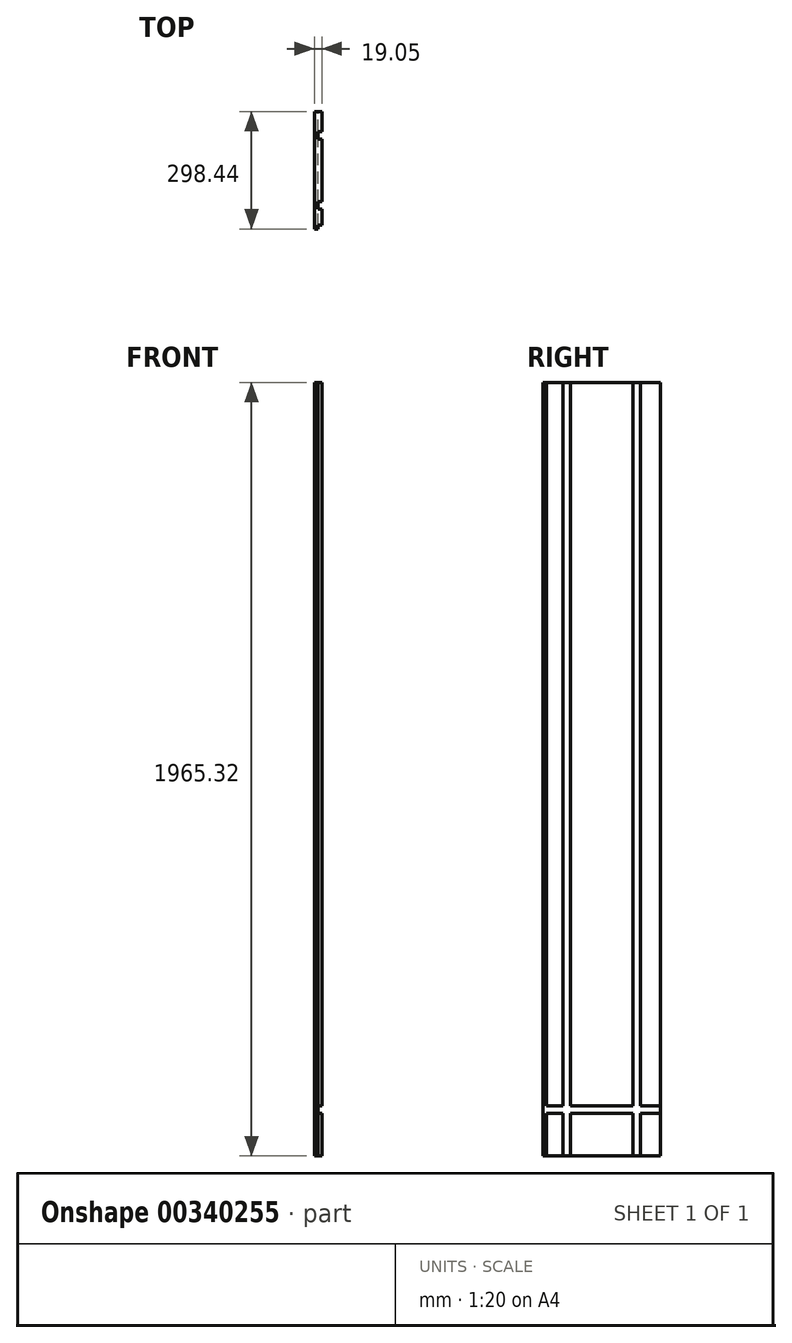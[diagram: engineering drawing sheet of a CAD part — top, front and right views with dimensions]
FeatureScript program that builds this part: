
annotation { "Feature Type Name" : "Feature", "Feature Type Description" : "" }
export const myFeature = defineFeature(function(context is Context, id is Id, definition is map)
    precondition{}
    {
        {
            var Q0;
            Q0=qCreatedBy(makeId("Right.planeOp"),FACE);
            var sketch = newSketch(context, id + "F0", { "sketchPlane" : qUnion([Q0])});
            skLineSegment(sketch, "E0.bottom", {"start": v(149.22, -982.66) * mm, "end": v(-149.23, -982.66) * mm});
            skLineSegment(sketch, "E0.top", {"start": v(149.22, 982.66) * mm, "end": v(-149.23, 982.66) * mm});
            skLineSegment(sketch, "E0.left", {"start": v(149.22, -982.66) * mm, "end": v(149.22, 982.66) * mm});
            skLineSegment(sketch, "E0.right", {"start": v(-149.23, -982.66) * mm, "end": v(-149.23, 982.66) * mm});
            skPoint(sketch, "E0.middle", {"position": v(0, 0) * mm});
            skSolve(sketch);
        }
        {
            var Q0;
            Q0=makeQuery(id+"F0.imprint","IMPRINT",FACE,{"disambiguationData":[TD([[makeQuery(id+"F0.imprint","IMPRINT",EDGE,{"derivedFrom":sQuery(id+"F0.wireOp",EDGE,"E0.bottom")}),-1.0]])]});
            extrude(context, id + "F1", {"entities" : qUnion([Q0]), "depth" : 19.05 * mm});
        }
        {
            var Q0;
            Q0=makeQuery(id+"F1.opExtrude","CAP_FACE",FACE,{"disambiguationData":[OSD([sQuery(id+"F0.wireOp",EDGE,"E0.bottom"),sQuery(id+"F0.wireOp",EDGE,"E0.top"),sQuery(id+"F0.wireOp",EDGE,"E0.left"),sQuery(id+"F0.wireOp",EDGE,"E0.right")])],"isStart":false});
            var sketch = newSketch(context, id + "F2", { "sketchPlane" : qUnion([Q0])});
            skLineSegment(sketch, "E1.bottom", {"start": v(-149.23, -855.66) * mm, "end": v(149.22, -855.66) * mm});
            skLineSegment(sketch, "E1.top", {"start": v(-149.23, -874.71) * mm, "end": v(149.22, -874.71) * mm});
            skLineSegment(sketch, "E1.left", {"start": v(-149.23, -855.66) * mm, "end": v(-149.23, -874.71) * mm});
            skLineSegment(sketch, "E1.right", {"start": v(149.22, -855.66) * mm, "end": v(149.22, -874.71) * mm});
            skSolve(sketch);
        }
        {
            var Q0;
            Q0 = qSketchRegion(id + "F2", true);
            extrude(context, id + "F3", {"entities" : qUnion([Q0]), "operationType" : NewBodyOperationType.REMOVE, "oppositeDirection" : true, "depth" : 9.52 * mm});
        }
        {
            var Q0;
            {var subQ0=sQuery(id+"F0.wireOp",EDGE,"E0.top");var subQ1=sQuery(id+"F0.wireOp",EDGE,"E0.left");var subQ2=sQuery(id+"F0.wireOp",EDGE,"E0.right");Q0=makeQuery(id+"F3.boolean.opBoolean","SPLIT",FACE,{"disambiguationData":[TD([makeQuery(id+"F1.opExtrude","SWEPT_FACE",FACE,{"disambiguationData":[OSD([subQ0])]})])],"derivedFrom":makeQuery(id+"F1.opExtrude","CAP_FACE",FACE,{"disambiguationData":[OSD([sQuery(id+"F0.wireOp",EDGE,"E0.bottom"),subQ0,subQ1,subQ2])],"isStart":false})});}
            var sketch = newSketch(context, id + "F4", { "sketchPlane" : qUnion([Q0])});
            skLineSegment(sketch, "E2.bottom", {"start": v(-98.43, 982.66) * mm, "end": v(-79.38, 982.66) * mm});
            skLineSegment(sketch, "E2.top", {"start": v(-98.43, -982.66) * mm, "end": v(-79.38, -982.66) * mm});
            skLineSegment(sketch, "E2.left", {"start": v(-98.43, 982.66) * mm, "end": v(-98.43, -982.66) * mm});
            skLineSegment(sketch, "E2.right", {"start": v(-79.38, 982.66) * mm, "end": v(-79.38, -982.66) * mm});
            skLineSegment(sketch, "E3", {"start": v(0, 982.66) * mm, "end": v(0, -982.66) * mm, "construction": true});
            skLineSegment(sketch, "E4.MirrorCS", {"start": v(98.43, -982.66) * mm, "end": v(79.38, -982.66) * mm});
            skLineSegment(sketch, "E5.MirrorCS", {"start": v(98.43, 982.66) * mm, "end": v(79.38, 982.66) * mm});
            skLineSegment(sketch, "E6.MirrorCS", {"start": v(79.38, 982.66) * mm, "end": v(79.38, -982.66) * mm});
            skLineSegment(sketch, "E7.MirrorCS", {"start": v(98.43, 982.66) * mm, "end": v(98.43, -982.66) * mm});
            skSolve(sketch);
        }
        {
            var Q0;
            Q0 = qSketchRegion(id + "F4", true);
            extrude(context, id + "F5", {"entities" : qUnion([Q0]), "operationType" : NewBodyOperationType.REMOVE, "oppositeDirection" : true, "depth" : 9.52 * mm});
        }
        {
            var Q0;
            Q0=makeQuery(id+"F1.opExtrude","SWEPT_FACE",FACE,{"disambiguationData":[OSD([sQuery(id+"F0.wireOp",EDGE,"E0.bottom")])]});
            var sketch = newSketch(context, id + "F6", { "sketchPlane" : qUnion([Q0])});
            skLineSegment(sketch, "E8.bottom", {"start": v(19.05, 149.23) * mm, "end": v(9.53, 149.23) * mm});
            skLineSegment(sketch, "E8.top", {"start": v(19.05, 139.7) * mm, "end": v(9.53, 139.7) * mm});
            skLineSegment(sketch, "E8.left", {"start": v(19.05, 149.23) * mm, "end": v(19.05, 139.7) * mm});
            skLineSegment(sketch, "E8.right", {"start": v(9.53, 149.23) * mm, "end": v(9.53, 139.7) * mm});
            skSolve(sketch);
        }
        {
            var Q0;
            Q0 = qSketchRegion(id + "F6", true);
            extrude(context, id + "F7", {"entities" : qUnion([Q0]), "operationType" : NewBodyOperationType.REMOVE, "endBound" : BoundingType.THROUGH_ALL, "oppositeDirection" : true, "depth" : 25.4 * mm});
        }
    });
